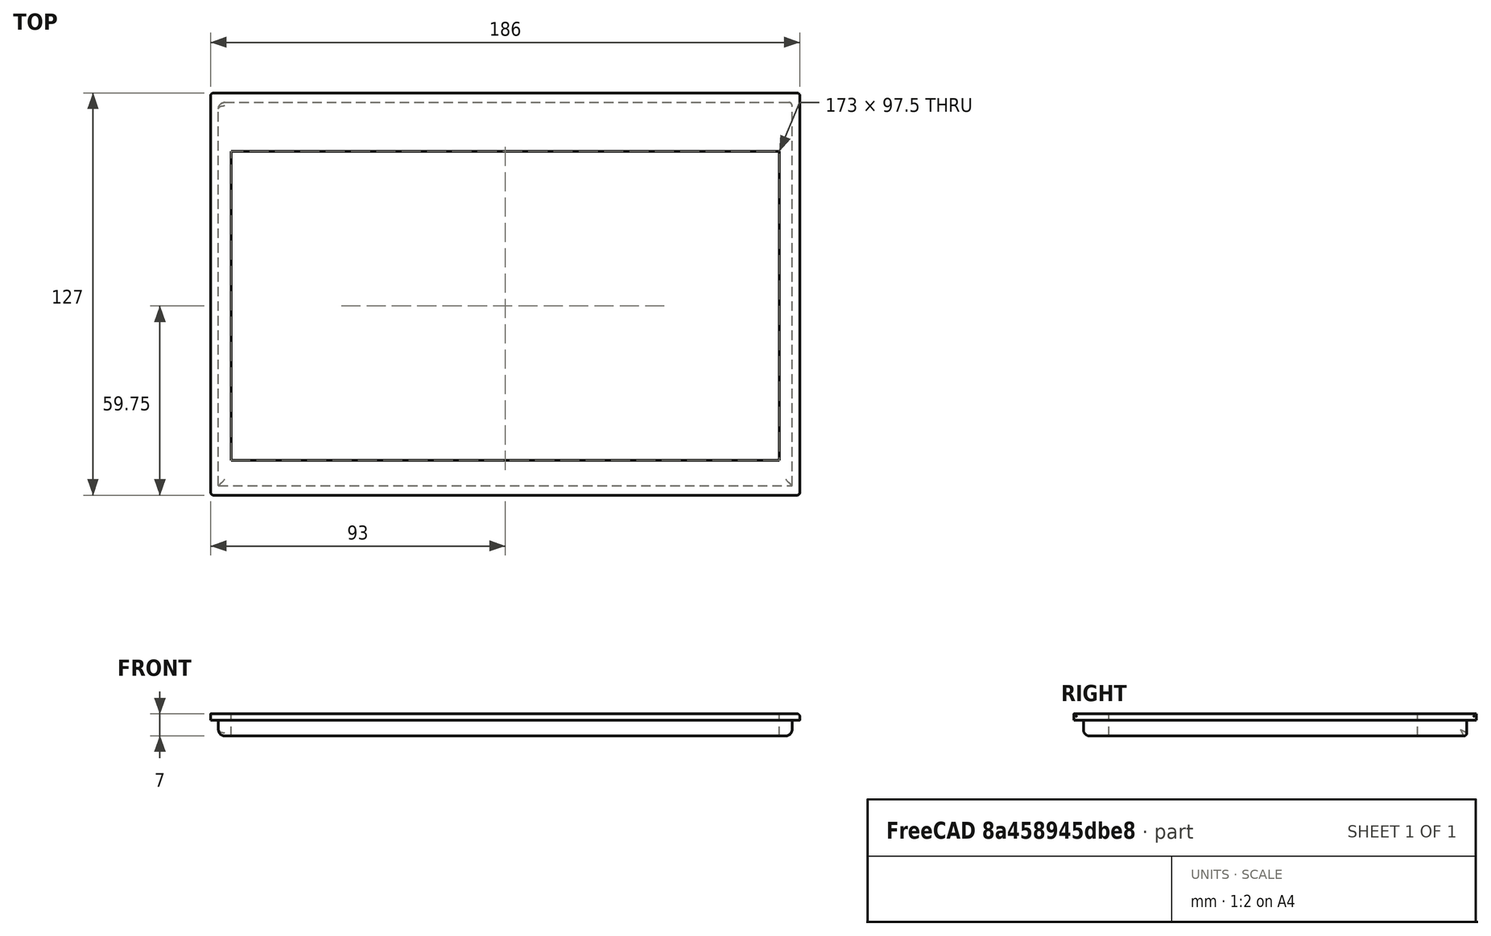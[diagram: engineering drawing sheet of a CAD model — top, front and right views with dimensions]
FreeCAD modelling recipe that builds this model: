
FCSTD DOCUMENT  (FreeCAD 0.19R24291 (Git))
Label: fascia-atoto-s8
License: All rights reserved
LicenseURL: http://en.wikipedia.org/wiki/All_rights_reserved
objects: Part::Box×3, Part::Fillet×2, Part::MultiFuse×1, Part::Cut×1
note: 7 computed .brp shape members not serialized (recipe doc carries the construction recipe); baked Part::Feature solids carry a one-line shape summary decoded from their .brp

FEATURE [Part::Box] Box017  label="Lip"
  AttacherType = Attacher::AttachEngine3D
  Height = 2
  Length = 186
  Width = 127
FEATURE [Part::Box] Box018  label="Cutout"
  AttacherType = Attacher::AttachEngine3D
  Height = 30
  Length = 173
  Placement = pos=(6.5,11,-25) rot=(0,0,1;0rad)
  Width = 97.5
FEATURE [Part::Box] Box019  label="Cube016"
  AttacherType = Attacher::AttachEngine3D
  Height = 5
  Length = 181
  Placement = pos=(2.5,3,-5) rot=(0,0,1;0rad)
  Width = 121
FEATURE [Part::MultiFuse] Fusion007
  Shapes = -> [Box017,Box019]
FEATURE [Part::Cut] Cut007
  Base = -> Fusion007
  Tool = -> Box018
FEATURE [Part::Fillet] Fillet008  label="Fill Plate"
  Base = -> Cut007
  Edges = 4 edges r=2: [Edge30,Edge31,Edge32,Edge35]
FEATURE [Part::Fillet] Fillet009  label="Fascia"
  Base = -> Fillet008
  Edges = 8 edges r=1: [Edge13,Edge16,Edge18,Edge21,Edge23,Edge24,Edge26,Edge28]
